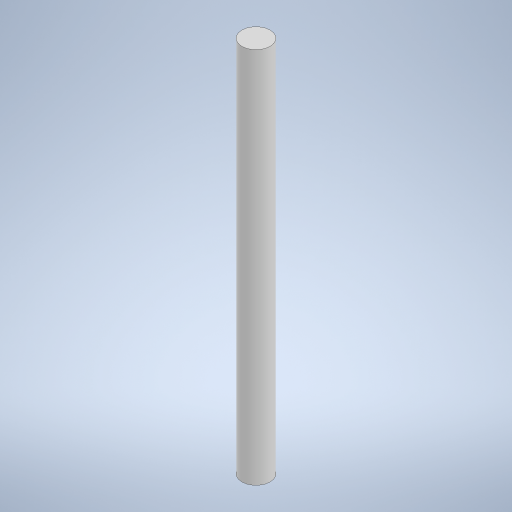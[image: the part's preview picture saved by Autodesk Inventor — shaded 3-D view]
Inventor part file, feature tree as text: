
AUTODESK INVENTOR PART (.ipt)
format: ipt  version: 2023 (Build 270158000, 158)  size: 226,304 bytes
history: native  units: in
note: dims shown in document units (in); Inventor stores cm internally (conversion verified against a paired STEP export)
features: extrude x1, sketch x1
ambient origin geometry x8: Origin, YZ Plane, XZ Plane, XY Plane, X Axis, Y Axis, Z Axis, Center Point
bodies: Solide1 (feature_tree)
feature tree (2):
  extrude  "Extrusion1"  Depth=0.1181in
  sketch  "Esquisse1"
